# Revit family: RONDO-90
name_source: partatom
category: Осветительные приборы
revit_build: Autodesk Revit 2017 (Build: 20160225_1515(x64)
units: mm (PartAtom-declared; Revit-internal decimal feet)

## family parameters
Всегда вертикально = Да
Источник света = Да
На основе рабочей плоскости = Нет
Общий = Нет
При загрузке вырезать с полостями = Нет
Размер круглого соединителя = Использовать диаметр
Тип детали = Нормальный
Точка расчета площади = Нет

## types (7) — shared parameters
ADSK_Единица измерения = шт.
ADSK_Завод-изготовитель = ARLIGHT
ADSK_Классификация нагрузок = Освещение
ADSK_Количество фаз = 1
ADSK_Количество фаз числовое = 1
ADSK_Коэффициент мощности = 0.5
ADSK_Масса_Текст = 0.42
ADSK_Наименование = Светильник
ADSK_Напряжение = 230 В
ADSK_Номинальная мощность = 8 Вт
ADSK_Полная мощность = 16 В·А
ADSK_Размер_Высота = 65 мм
ADSK_Размер_Диаметр = 90 мм
ADSK_Ток = 0 А
ARL_Драйвер = Встроенный (300mA 20-40V)
ARL_Индекс цветопередачи = >80
ARL_Класс защиты от поражения электрическим током = II
ARL_Класс пылевлагозащиты = IP40
ARL_Область использования = Для освещения в жилых, офисных, торговых помещений.
ARL_Рабочая температура окружающей среды = -10...+50 °C
ARL_Серия = RONDO
ARL_Способ монтажа = Накладной
ARL_Тип товара = Светильник
ARL_Угол обзора = 100°
URL = https://arlight.ru
Видимая форма излучения при визуализации = Нет
Группа модели = Светильники
Изготовитель = ARLIGHT
Изготовитель (сайт) = www.arlight.ru
Изготовитель (телефон) = 8 800 505 26 29
Излучение по диаметру окружности = 88 мм
Полная установленная мощность = 16 В·А
Разработчик = НТЦ Конструктор
Разработчик (URL) = https://constructor.ru
Разработчик (телефон) = +7 (495) 781-05-35
Светофильтр = 16777215
Смещение цветовой температуры при затухании лампы = <Нет>
Угол наклона = 90.00°

## per-type parameters (varying)
| type | ADSK_Код изделия | ADSK_Марка | ARL_Материал корпуса | ARL_Обозначение корпуса | ARL_Цвет покрытия | ARL_Цвет свечения | Комментарии к типоразмеру | Описание | Файл фотометрической сетки |
| 022901 Светильник SP-RONDO-90B-8W Warm White | Арт. 022901 | SP-RONDO-90B-8W Warm White | Металл, чёрный | Корпус круглый, металл, цвет черный | Черный | Теплый 3000K | Арт. 022901 | Накладной светильник 8 Вт, черный круглый корпус. Цвет ТЕПЛЫЙ БЕЛЫЙ 3000K, св.поток 480-560лм, CRI(Ra)>80, угол 100°. Размер Ф90x65 мм. Питание AC176-240V, 8 Вт, драйвер встроенный (300mA 20-40V). | 022901_SP-RONDO-90B-8W Warm White.ies |
| 022241 Светильник SP-RONDO-90B-8W Day White | Арт. 022241 | SP-RONDO-90B-8W Day White | Металл, чёрный | Корпус круглый, металл, цвет черный | Черный | Дневной 4000K | Арт. 022241 | Накладной светильник 8 Вт, черный круглый корпус. Цвет ДНЕВНОЙ БЕЛЫЙ 4000K, св.поток 480-560лм, CRI(Ra)>80, угол 100°. Размер Ф90x65 мм. Питание AC176-240V, 8 Вт, драйвер встроенный (300mA 20-40V). | 022241_SP-RONDO-90B-8W Day White.ies |
| 022907 Светильник SP-RONDO-90B-8W White | Арт. 022907 | SP-RONDO-90B-8W White | Металл, чёрный | Корпус круглый, металл, цвет черный | Черный | Белый 6000K | Арт. 022907 | Накладной светильник 8 Вт, черный круглый корпус. Цвет БЕЛЫЙ 6000K, св.поток 480-560лм, CRI(Ra)>80, угол 100°. Размер Ф90x65 мм. Питание AC176-240V, 8 Вт, драйвер встроенный (300mA 20-40V). | 022907_SP-RONDO-90B-8W White.ies |
| 022907(1) Светильник SP-RONDO-90B-8W White | Арт. 022907(1) | SP-RONDO-90B-8W White | Металл, чёрный | Корпус круглый, металл, цвет черный | Черный | Белый 6000K | Арт. 022907(1) | Накладной светильник 8 Вт, черный круглый корпус. Цвет БЕЛЫЙ 6000K, св.поток 480-560лм, CRI(Ra)>80, угол 100°. Размер Ф90x65 мм. Питание AC176-240V, 8 Вт, драйвер встроенный (300mA 20-40V). | 022907(1)_SP-RONDO-90B-8W White.ies |
| 021780 Светильник SP-RONDO-90A-8W Warm White | Арт. 021780 | SP-RONDO-90A-8W Warm White | Металл, белый | Корпус круглый, металл, цвет белый | Белый | Теплый 3000K | Арт. 021780 | Накладной светильник 8 Вт, белый круглый корпус. Цвет ТЕПЛЫЙ БЕЛЫЙ 3000K, св.поток 480-560лм, CRI(Ra)>80, угол 100°. Размер Ф90x65 мм. Питание AC176-240V, 8 Вт, драйвер встроенный (300mA 20-40V). | 021780_SP-RONDO-90A-8W Warm White.ies |
| 022234 Светильник SP-RONDO-90A-8W Day White | Арт. 022234 | SP-RONDO-90A-8W Day White | Металл, белый | Корпус круглый, металл, цвет белый | Белый | Дневной 4000K | Арт. 022234 | Накладной светильник 8 Вт, белый круглый корпус. Цвет ДНЕВНОЙ БЕЛЫЙ 4000K, св.поток 480-560лм, CRI(Ra)>80, угол 100°. Размер Ф90x65 мм. Питание AC176-240V, 8 Вт, драйвер встроенный (300mA 20-40V). | 022234_SP-RONDO-90A-8W Day White.ies |
| 022235 Светильник SP-RONDO-90A-8W White | Арт. 022235 | SP-RONDO-90A-8W White | Металл, белый | Корпус круглый, металл, цвет белый | Белый | Белый 6000K | Арт. 022235 | Накладной светильник 8 Вт, белый круглый корпус. Цвет БЕЛЫЙ 6000K, св.поток 480-560лм, CRI(Ra)>80, угол 100°. Размер Ф90x65 мм. Питание AC176-240V, 8 Вт, драйвер встроенный (300mA 20-40V). | 022235_SP-RONDO-90A-8W White.ies |
